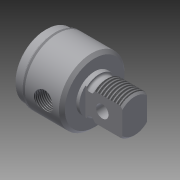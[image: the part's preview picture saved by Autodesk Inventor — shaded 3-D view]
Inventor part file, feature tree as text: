
AUTODESK INVENTOR PART (.ipt)
format: ipt  version: 2014 SP2 (Build 180246200, 246)  size: 299,008 bytes
history: native  units: in
note: dims shown in document units (in); Inventor stores cm internally (conversion verified against a paired STEP export)
features: other x154, sketch x8, revolve x5, thread x2, extrude x2, hole x1
ambient origin geometry x8: Origin, YZ Plane, XZ Plane, XY Plane, X Axis, Y Axis, Z Axis, Center Point
bodies: Solid1 (feature_tree)
feature tree (172):
  revolve  "Revolution1"  Angle=360.0deg
  revolve  "Revolution2"  [1 undecoded]
  thread  "Thread1"  [1 undecoded]
  extrude  "Extrusion1"  TaperAngle=360.0deg  [1 undecoded]
  hole  "Hole1"  [1 undecoded]
  revolve  "Revolution3"  [1 undecoded]
  thread  "Thread2"  [1 undecoded]
  revolve  "Revolution4"  [1 undecoded]
  revolve  "Revolution5"  [1 undecoded]
  extrude  "Extrusion2"  [1 undecoded]
  other  "1_XY"
  other  "1_YZ"
  other  "1_ZX"
  other  "1_X"
  other  "1_Y"
  other  "1_Z"
  other  "1_Center"
  other  "c1_XY"
  other  "c1_YZ"
  other  "c1_ZX"
  other  "c1_X"
  other  "c1_Y"
  other  "c1_Z"
  other  "c1_Center"
  other  "c2_XY"
  other  "c2_YZ"
  other  "c2_ZX"
  other  "c2_X"
  other  "c2_Y"
  other  "c2_Z"
  other  "c2_Center"
  other  "cc1_XY"
  other  "cc1_YZ"
  other  "cc1_ZX"
  other  "cc1_X"
  other  "cc1_Y"
  other  "cc1_Z"
  other  "cc1_Center"
  other  "cc2_XY"
  other  "cc2_YZ"
  other  "cc2_ZX"
  other  "cc2_X"
  other  "cc2_Y"
  other  "cc2_Z"
  other  "cc2_Center"
  other  "lovra1_XY"
  other  "lovra1_YZ"
  other  "lovra1_ZX"
  other  "lovra1_X"
  other  "lovra1_Y"
  other  "lovra1_Z"
  other  "lovra1_Center"
  other  "lovra2_XY"
  other  "lovra2_YZ"
  other  "lovra2_ZX"
  other  "lovra2_X"
  other  "lovra2_Y"
  other  "lovra2_Z"
  other  "lovra2_Center"
  other  "lovra21_XY"
  other  "lovra21_YZ"
  other  "lovra21_ZX"
  other  "lovra21_X"
  other  "lovra21_Y"
  other  "lovra21_Z"
  other  "lovra21_Center"
  other  "lovra22_XY"
  other  "lovra22_YZ"
  other  "lovra22_ZX"
  other  "lovra22_X"
  other  "lovra22_Y"
  other  "lovra22_Z"
  other  "lovra22_Center"
  other  "lovra3_XY"
  other  "lovra3_YZ"
  other  "lovra3_ZX"
  other  "lovra3_X"
  other  "lovra3_Y"
  other  "lovra3_Z"
  other  "lovra3_Center"
  other  "olen_XY"
  other  "olen_YZ"
  other  "olen_ZX"
  other  "olen_X"
  other  "olen_Y"
  other  "olen_Z"
  other  "olen_Center"
  other  "p1_XY"
  other  "p1_YZ"
  other  "p1_ZX"
  other  "p1_X"
  other  "p1_Y"
  other  "p1_Z"
  other  "p1_Center"
  other  "p2_XY"
  other  "p2_YZ"
  other  "p2_ZX"
  other  "p2_X"
  other  "p2_Y"
  other  "p2_Z"
  other  "p2_Center"
  other  "port_XY"
  other  "port_YZ"
  other  "port_ZX"
  other  "port_X"
  other  "port_Y"
  other  "port_Z"
  other  "port_Center"
  other  "port2_XY"
  other  "port2_YZ"
  other  "port2_ZX"
  other  "port2_X"
  other  "port2_Y"
  other  "port2_Z"
  other  "port2_Center"
  other  "thd1_XY"
  other  "thd1_YZ"
  other  "thd1_ZX"
  other  "thd1_X"
  other  "thd1_Y"
  other  "thd1_Z"
  other  "thd1_Center"
  other  "thd2_XY"
  other  "thd2_YZ"
  other  "thd2_ZX"
  other  "thd2_X"
  other  "thd2_Y"
  other  "thd2_Z"
  other  "thd2_Center"
  other  "to_mounting_bracket_XY"
  other  "to_mounting_bracket_YZ"
  other  "to_mounting_bracket_ZX"
  other  "to_mounting_bracket_X"
  other  "to_mounting_bracket_Y"
  other  "to_mounting_bracket_Z"
  other  "to_mounting_bracket_Center"
  other  "to_nut_XY"
  other  "to_nut_YZ"
  other  "to_nut_ZX"
  other  "to_nut_X"
  other  "to_nut_Y"
  other  "to_nut_Z"
  other  "to_nut_Center"
  other  "to_pin_XY"
  other  "to_pin_YZ"
  other  "to_pin_ZX"
  other  "to_pin_X"
  other  "to_pin_Y"
  other  "to_pin_Z"
  other  "to_pin_Center"
  other  "to_screw_XY"
  other  "to_screw_YZ"
  other  "to_screw_ZX"
  other  "to_screw_X"
  other  "to_screw_Y"
  other  "to_screw_Z"
  other  "to_screw_Center"
  other  "to_tube_XY"
  other  "to_tube_YZ"
  other  "to_tube_ZX"
  other  "to_tube_X"
  other  "to_tube_Y"
  other  "to_tube_Z"
  other  "to_tube_Center"
  sketch  "Sketch_18"  dims[d14=0.2731in d15=0.0in d16=360.0deg]
  sketch  "Sketch_15"  dims[d6=0.5in d7=0.75in d8=0.375in d9=0.25in d10=0.5635in d11=0.8932in d12=120.0deg d13=360.0deg]
  sketch  "Sketch_9"  dims[d2=0.5195in d3=0.0in d4=0.75in d5=0.0in]
  sketch  "Sketch4"  dims[d0=360.0deg d1=360.0deg]
  sketch  "Sketch_68"
  sketch  "Sketch_20"  dims[d17=360.0deg d18=0.75in d19=0.0in]
  sketch  "Sketch_24"  dims[d20=0.0in d21=0.0in d22=0.0in d23=0.0in d24=0.0in d25=0.0in d26=0.0in d27=0.0in]
  sketch  "Sketch_43"
note: 9 required parameter values undecoded (feature->parameter linkage not recoverable at this tier; creation-order binding heuristic only, values carry confidence <= 0.55)